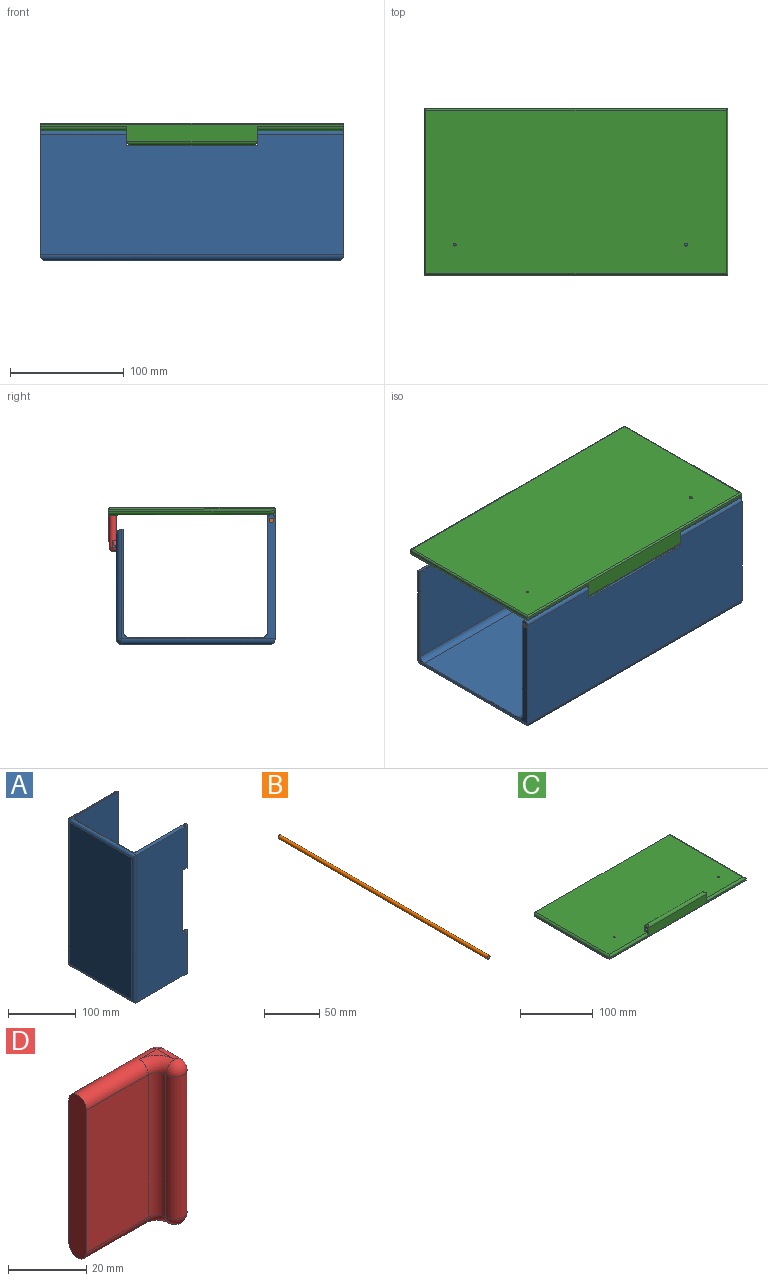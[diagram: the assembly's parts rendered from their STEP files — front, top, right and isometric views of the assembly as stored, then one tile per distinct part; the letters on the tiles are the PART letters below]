
ASSEMBLY  parts=4 mates=3
PART A: 35 faces, bbox 114.3x139.7x266.7 mm
  f0: plane 114.3x6.35mm, normal (1,0,0), area 725.8mm2, adj f3,f6,f29,f30
  f1: plane 134.62x109.22mm, normal (0,0,1), area 972.8mm2, adj f3,f4,f6,f8,f9,f10,f11,f21
  f2: plane 134.62x109.22mm, normal (0,0,-1), area 972.8mm2, adj f3,f4,f6,f8,f9,f10,f11,f23
  f3: plane 266.7x99.7mm, normal (0,1,0), area 25499.9mm2, adj f0,f1,f2,f9,f29,f30,f33,f34
  f4: plane 266.7x90.17mm, normal (0,-1,0), area 23661.2mm2, adj f1,f2,f10,f11,f12,f13,f14,f15
  f5: plane 256.54x129.54mm, normal (-1,0,0), area 33232.2mm2, adj f20,f21,f22,f23
  f6: plane 266.7x106.05mm, normal (0,-1,0), area 27193.5mm2, adj f0,f1,f2,f20,f29,f30,f33,f34
  f7: plane 256.54x91.44mm, normal (0,1,0), area 22374.1mm2, adj f16,f17,f18,f19,f22,f26,f27,f28
  f8: plane 266.7x116.84mm, normal (1,0,0), area 31161.2mm2, adj f1,f2,f9,f10
  f9: cylinder r=5.08mm len=266.7mm, axis (0,0,-1), area 2128.2mm2, adj f1,f2,f3,f8
  f10: cylinder r=5.08mm len=266.7mm, axis (0,0,1), area 2128.2mm2, adj f1,f2,f4,f8
  f11: plane 266.7x1.27mm, normal (1,0,0), area 338.7mm2, adj f1,f2,f4,f28
  f12: plane 50.8x1.27mm, normal (-1,0,0), area 64.5mm2, adj f4,f13,f15,f16
  f13: plane 7.62x1.27mm, normal (0,0,1), area 9.7mm2, adj f4,f12,f14,f18
  f14: plane 50.8x1.27mm, normal (1,0,0), area 64.5mm2, adj f4,f13,f15,f19
  f15: plane 7.62x1.27mm, normal (0,0,-1), area 9.7mm2, adj f4,f12,f14,f17
  f16: cylinder r=5.08mm len=60.96mm, axis (0,0,-1), area 434.8mm2, adj f7,f12,f17,f18
  f17: cylinder r=5.08mm len=17.78mm, axis (1,0,0), area 90.3mm2, adj f7,f15,f16,f19
  f18: cylinder r=5.08mm len=17.78mm, axis (-1,0,0), area 90.3mm2, adj f7,f13,f16,f19
  f19: cylinder r=5.08mm len=60.96mm, axis (0,0,1), area 434.8mm2, adj f7,f14,f17,f18
  f20: cylinder r=5.08mm len=266.7mm, axis (0,0,1), area 2098.7mm2, adj f5,f6,f21,f23
  f21: cylinder r=5.08mm len=134.62mm, axis (0,-1,0), area 1059.5mm2, adj f1,f5,f20,f24
  f22: cylinder r=5.08mm len=256.54mm, axis (0,0,-1), area 2047.1mm2, adj f5,f7,f24,f25
  f23: cylinder r=5.08mm len=134.62mm, axis (0,1,0), area 1059.5mm2, adj f2,f5,f20,f25
  f24: sphere r=5.08mm, area 40.5mm2, adj f21,f22,f26
  f25: sphere r=5.08mm, area 40.5mm2, adj f22,f23,f27
  f26: cylinder r=5.08mm len=96.52mm, axis (-1,0,0), area 755.5mm2, adj f1,f7,f24,f28
  f27: cylinder r=5.08mm len=96.52mm, axis (1,0,0), area 755.5mm2, adj f2,f7,f25,f28
  f28: cylinder r=5.08mm len=266.7mm, axis (0,0,1), area 2098.7mm2, adj f7,f11,f26,f27
  f29: plane 12.7x6.35mm, normal (0,0,-1), area 64.9mm2, adj f0,f3,f6,f32,f34
  f30: plane 12.7x6.35mm, normal (0,0,1), area 64.9mm2, adj f0,f3,f6,f31,f33
  f31: cylinder r=1.91mm len=76.2mm, axis (0,0,-1), area 912.1mm2, adj f2,f30
  f32: cylinder r=1.91mm len=76.2mm, axis (0,0,-1), area 912.1mm2, adj f1,f29
  f33: cylinder r=3.17mm len=76.2mm, axis (0,0,-1), area 760.1mm2, adj f2,f3,f6,f30
  f34: cylinder r=3.17mm len=76.2mm, axis (0,0,-1), area 760.1mm2, adj f1,f3,f6,f29
PART B: 3 faces, bbox 3.8x266.7x3.8 mm
  f0: cylinder r=1.91mm len=266.7mm, axis (0,1,0), area 3192.3mm2, adj f1,f2
  f1: plane 3.81x3.81mm, normal (0,-1,0), area 11.4mm2, adj f0
  f2: plane 3.81x3.81mm, normal (0,1,0), area 11.4mm2, adj f0
PART C: 23 faces, bbox 266.7x146.1x19.1 mm
  f0: plane 146.05x1.91mm, normal (1,0,0), area 278.2mm2, adj f1,f3,f16,f17
  f1: plane 266.7x5.08mm, normal (0,1,0), area 1350.5mm2, adj f0,f2,f4,f14,f16,f18
  f2: plane 146.05x1.91mm, normal (-1,0,0), area 278.2mm2, adj f1,f3,f14,f20
  f3: plane 266.7x14.61mm, normal (0,-1,0), area 1959.7mm2, adj f0,f2,f6,f8,f11,f13,f15,f19
  f4: plane 260.35x142.88mm, normal (0,0,1), area 36824.5mm2, adj f1,f6,f7,f8,f13,f14,f15,f16
  f5: plane 264.16x143.51mm, normal (0,0,-1), area 37899.5mm2, adj f17,f18,f19,f20,f21,f22
  f6: plane 12.7x6.35mm, normal (-1,0,0), area 51.2mm2, adj f3,f4,f7,f9,f10,f13
  f7: plane 114.3x9.53mm, normal (0,1,0), area 1088.7mm2, adj f4,f6,f8,f11
  f8: plane 12.7x6.35mm, normal (1,0,0), area 51.2mm2, adj f3,f4,f7,f9,f12,f15
  f9: cylinder r=1.91mm len=114.3mm, axis (1,0,0), area 1368.1mm2, adj f6,f8
  f10: cylinder r=3.17mm len=6.35mm, axis (0,1,0), area 20.2mm2, adj f6,f11
  f11: cylinder r=3.17mm len=114.3mm, axis (1,0,0), area 1117.1mm2, adj f3,f7,f10,f12
  f12: cylinder r=3.17mm len=6.35mm, axis (0,-1,0), area 20.2mm2, adj f8,f11
  f13: cylinder r=3.17mm len=76.2mm, axis (-1,0,0), area 374.3mm2, adj f3,f4,f6,f14
  f14: cylinder r=3.17mm len=146.05mm, axis (0,1,0), area 722.6mm2, adj f1,f2,f4,f13
  f15: cylinder r=3.17mm len=76.2mm, axis (-1,0,0), area 374.3mm2, adj f3,f4,f8,f16
  f16: cylinder r=3.17mm len=146.05mm, axis (0,-1,0), area 722.6mm2, adj f0,f1,f4,f15
  f17: cylinder r=1.27mm len=146.05mm, axis (0,1,0), area 289.5mm2, adj f0,f5,f18,f19
  f18: cylinder r=1.27mm len=266.7mm, axis (-1,0,0), area 530.2mm2, adj f1,f5,f17,f20
  f19: cylinder r=1.27mm len=266.7mm, axis (1,0,0), area 530.2mm2, adj f3,f5,f17,f20
  f20: cylinder r=1.27mm len=146.05mm, axis (0,-1,0), area 289.5mm2, adj f2,f5,f18,f19
  f21: cylinder r=1.27mm len=6.35mm, axis (0,0,-1), area 50.7mm2, adj f4,f5
  f22: cylinder r=1.27mm len=6.35mm, axis (0,0,-1), area 50.7mm2, adj f4,f5
PART D: 19 faces, bbox 31.8x12.7x50.8 mm
  f0: plane 44.45x22.23mm, normal (0,-1,0), area 987.9mm2, adj f4,f7,f9,f14
  f1: plane 6.35x6.35mm, normal (0,0,-1), area 8.7mm2, adj f9,f11,f12
  f2: plane 44.45x6.35mm, normal (1,0,0), area 282.3mm2, adj f6,f8,f12,f18
  f3: plane 6.35x6.35mm, normal (0,0,1), area 8.7mm2, adj f14,f15,f18
  f4: plane 50.8x6.35mm, normal (-1,0,0), area 313.9mm2, adj f0,f5,f9,f14
  f5: plane 44.45x28.58mm, normal (0,1,0), area 1270.2mm2, adj f4,f8,f9,f14
  f6: cylinder r=3.17mm len=44.45mm, axis (0,0,-1), area 443.4mm2, adj f2,f7,f13,f17
  f7: cylinder r=3.17mm len=44.45mm, axis (0,0,1), area 221.7mm2, adj f0,f6,f11,f15
  f8: cylinder r=3.17mm len=44.45mm, axis (0,0,1), area 221.7mm2, adj f2,f5,f10,f16
  f9: cylinder r=3.17mm len=28.58mm, axis (1,0,0), area 253.4mm2, adj f0,f1,f4,f5,f10,f11
  f10: sphere r=3.17mm, area 15.8mm2, adj f8,f9,f12
  f11: torus R=6.35mm, axis (0,0,1), area 33.9mm2, adj f1,f7,f9,f13
  f12: cylinder r=3.17mm len=6.35mm, axis (0,-1,0), area 31.7mm2, adj f1,f2,f10,f13
  f13: sphere r=3.17mm, area 31.7mm2, adj f6,f11,f12
  f14: cylinder r=3.17mm len=28.58mm, axis (1,0,0), area 253.4mm2, adj f0,f3,f4,f5,f15,f16
  f15: torus R=6.35mm, axis (0,0,1), area 33.9mm2, adj f3,f7,f14,f17
  f16: sphere r=3.17mm, area 15.8mm2, adj f8,f14,f18
  f17: sphere r=3.17mm, area 31.7mm2, adj f6,f15,f18
  f18: cylinder r=3.17mm len=6.35mm, axis (0,1,0), area 31.7mm2, adj f2,f3,f16,f17
PLACE A rot(axis=(0,-1,0),90deg) t=(-133.35,69.85,127)mm
PLACE B rot(axis=(0.58,-0.58,0.58),120deg) t=(-133.35,-66.67,109.22)mm
PLACE C rot(axis=(0,1,0),180deg) t=(133.35,-69.82,120.66)mm
PLACE D rot(axis=(0,1,0),90deg) t=(-25.4,76.13,82.18)mm
MATE revolute B.f0 <-> A.f31  axis (1,0,0) through (133.35,-66.67,109.22)mm
MATE fastened C.f4 <-> D.f4  axis (0,0,-1) through (0,73.04,113.94)mm
MATE revolute C.f9 <-> A.f31  axis (-1,0,0) through (-57.15,-66.67,109.22)mm
